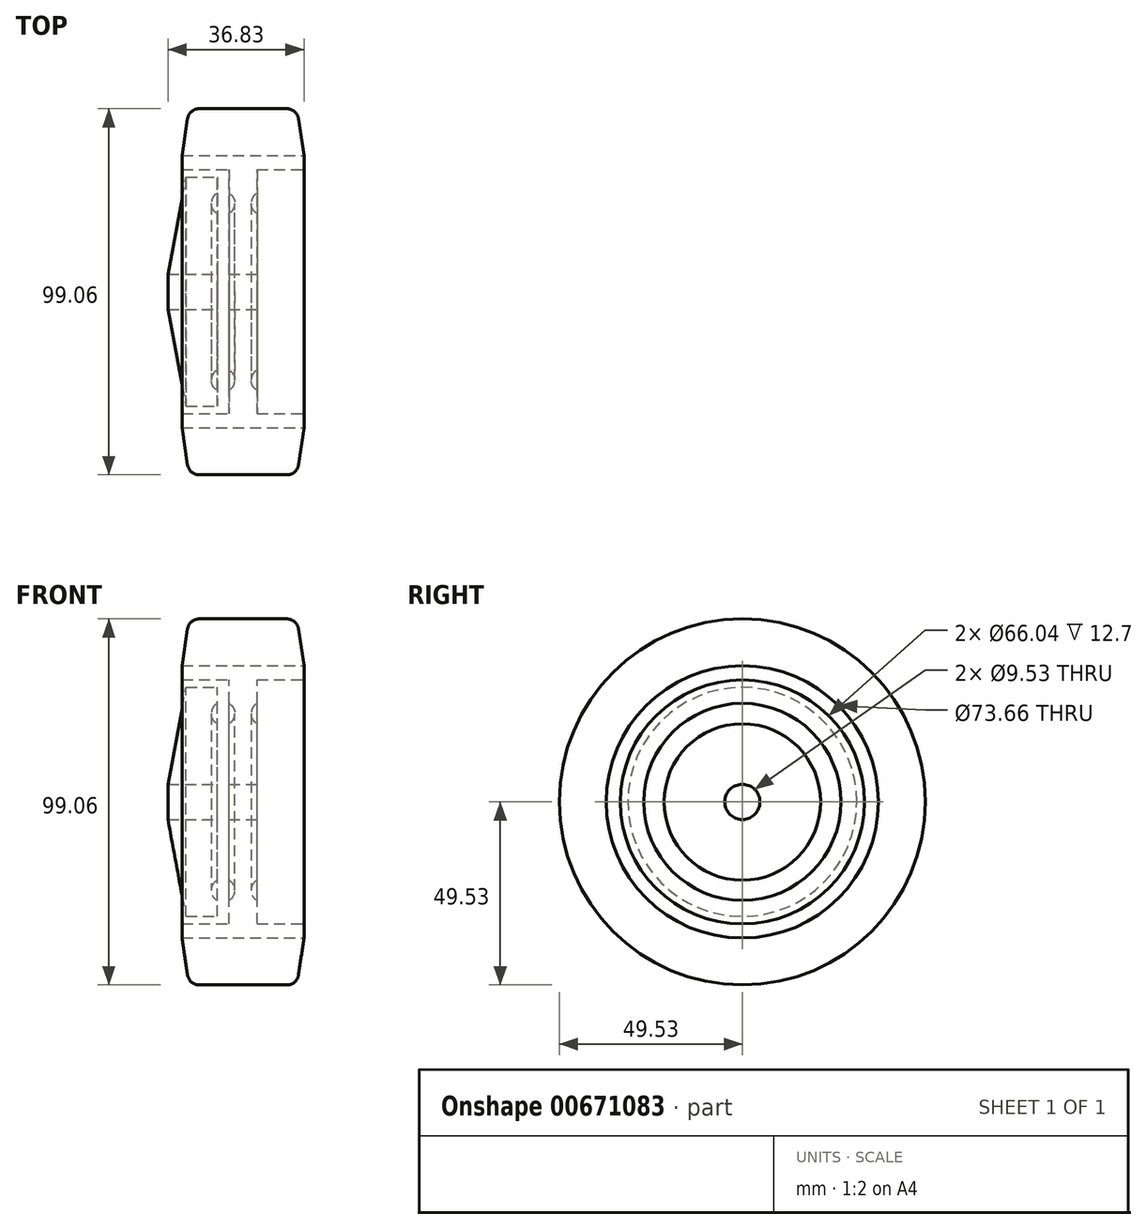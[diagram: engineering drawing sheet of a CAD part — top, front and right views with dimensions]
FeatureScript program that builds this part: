
annotation { "Feature Type Name" : "Feature", "Feature Type Description" : "" }
export const myFeature = defineFeature(function(context is Context, id is Id, definition is map)
    precondition{}
    {
        {
            var Q0;
            Q0=qCreatedBy(makeId("Top.planeOp"),FACE);
            var sketch = newSketch(context, id + "F0", { "sketchPlane" : qUnion([Q0])});
            skLineSegment(sketch, "E0", {"start": v(163.96, 0) * mm, "end": v(-163.85, 0) * mm, "construction": true});
            skSolve(sketch);
        }
        {
            var Q0;
            Q0=qCreatedBy(makeId("Front.planeOp"),FACE);
            var sketch = newSketch(context, id + "F1", { "sketchPlane" : qUnion([Q0])});
            skLineSegment(sketch, "E1", {"start": v(0, 0) * mm, "end": v(0, 60.9) * mm, "construction": true});
            skLineSegment(sketch, "E2", {"start": v(0, 49.53) * mm, "end": v(14.6, 49.53) * mm});
            skLineSegment(sketch, "E3", {"start": v(14.6, 49.53) * mm, "end": v(16.51, 36.83) * mm});
            skLineSegment(sketch, "E4", {"start": v(16.51, 36.83) * mm, "end": v(0, 36.83) * mm});
            skLineSegment(sketch, "E5.MirrorCS", {"start": v(0, 49.53) * mm, "end": v(-14.6, 49.53) * mm});
            skLineSegment(sketch, "E6.MirrorCS", {"start": v(-14.6, 49.53) * mm, "end": v(-16.51, 36.83) * mm});
            skLineSegment(sketch, "E7.MirrorCS", {"start": v(-16.51, 36.83) * mm, "end": v(0, 36.83) * mm});
            skSolve(sketch);
        }
        {
            var Q0;
            Q0=makeQuery(id+"F1.imprint","IMPRINT",FACE,{"disambiguationData":[TD([[makeQuery(id+"F1.imprint","IMPRINT",EDGE,{"derivedFrom":sQuery(id+"F1.wireOp",EDGE,"E2")}),-1.0]])]});
            var Q1;
            Q1=sQuery(id+"F0.wireOp",EDGE,"E0");
            revolve(context, id + "F2", {"entities" : qUnion([Q0]), "axis" : qUnion([Q1]), "revolveType" : RevolveType.FULL});
        }
        {
            var Q0;
            Q0=makeQuery(id+"F2.opRevolve","SWEPT_EDGE",EDGE,{"disambiguationData":[OSD([sQuery(id+"F1.wireOp",EDGE,"E5.MirrorCS"),sQuery(id+"F1.wireOp",EDGE,"E6.MirrorCS")])]});
            var Q1;
            Q1=makeQuery(id+"F2.opRevolve","SWEPT_EDGE",EDGE,{"disambiguationData":[OSD([sQuery(id+"F1.wireOp",EDGE,"E2"),sQuery(id+"F1.wireOp",EDGE,"E3")])]});
            fillet(context, id + "F3", {"entities" : qUnion([Q0, Q1]), "radius" : 3.17 * mm, "tangentPropagation" : true, "allowEdgeOverflow" : false});
        }
        {
            var Q0;
            Q0=qCreatedBy(makeId("Front.planeOp"),FACE);
            var sketch = newSketch(context, id + "F4", { "sketchPlane" : qUnion([Q0])});
            skPoint(sketch, "E8.0", {"position": v(16.51, 36.83) * mm});
            skPoint(sketch, "E9.0", {"position": v(0, 36.83) * mm});
            skLineSegment(sketch, "E10", {"start": v(0, 36.83) * mm, "end": v(16.51, 36.83) * mm});
            skLineSegment(sketch, "E11", {"start": v(16.51, 33.02) * mm, "end": v(16.51, 36.83) * mm});
            skLineSegment(sketch, "E12", {"start": v(16.51, 33.02) * mm, "end": v(3.81, 33.02) * mm});
            skLineSegment(sketch, "E13", {"start": v(3.81, 33.02) * mm, "end": v(3.81, 26.67) * mm});
            skArc(sketch, "E14", {"start": v(3.8, 26.67) * mm, "mid": v(2.22, 23.92) * mm, "end": v(3.81, 21.17) * mm});
            skLineSegment(sketch, "E15.MirrorCS", {"start": v(0, 36.83) * mm, "end": v(-16.51, 36.83) * mm});
            skLineSegment(sketch, "E16.MirrorCS", {"start": v(-16.51, 33.02) * mm, "end": v(-16.51, 36.83) * mm});
            skLineSegment(sketch, "E17.MirrorCS", {"start": v(-16.51, 33.02) * mm, "end": v(-3.81, 33.02) * mm});
            skLineSegment(sketch, "E18.MirrorCS", {"start": v(-3.81, 33.02) * mm, "end": v(-3.81, 26.67) * mm});
            skArc(sketch, "E19.MirrorCS", {"start": v(-3.8, 26.67) * mm, "mid": v(-2.22, 23.92) * mm, "end": v(-3.81, 21.17) * mm});
            skLineSegment(sketch, "E20", {"start": v(3.81, 21.17) * mm, "end": v(3.81, 4.76) * mm});
            skLineSegment(sketch, "E21", {"start": v(3.81, 4.76) * mm, "end": v(0, 4.76) * mm});
            skLineSegment(sketch, "E22.MirrorCS", {"start": v(-3.81, 21.17) * mm, "end": v(-3.81, 4.76) * mm});
            skLineSegment(sketch, "E23.MirrorCS", {"start": v(-3.81, 4.76) * mm, "end": v(0, 4.76) * mm});
            skSolve(sketch);
        }
        {
            var Q0;
            Q0=makeQuery(id+"F4.imprint","IMPRINT",FACE,{"disambiguationData":[TD([[makeQuery(id+"F4.imprint","IMPRINT",EDGE,{"derivedFrom":sQuery(id+"F4.wireOp",EDGE,"E10")}),-1.0]])]});
            var Q1;
            Q1=sQuery(id+"F0.wireOp",EDGE,"E0");
            revolve(context, id + "F5", {"entities" : qUnion([Q0]), "axis" : qUnion([Q1]), "revolveType" : RevolveType.FULL});
        }
        {
            var Q0;
            Q0=qCreatedBy(makeId("Front.planeOp"),FACE);
            var sketch = newSketch(context, id + "F6", { "sketchPlane" : qUnion([Q0])});
            skLineSegment(sketch, "E24", {"start": v(-6.99, 30.99) * mm, "end": v(-15.44, 30.99) * mm});
            skLineSegment(sketch, "E25", {"start": v(-15.44, 30.99) * mm, "end": v(-20.32, 4.76) * mm});
            skLineSegment(sketch, "E26", {"start": v(-20.32, 4.76) * mm, "end": v(-6.99, 4.76) * mm});
            skLineSegment(sketch, "E27", {"start": v(-6.99, 4.76) * mm, "end": v(-6.99, 21.17) * mm});
            skPoint(sketch, "E28.0", {"position": v(-3.8, 26.67) * mm});
            skLineSegment(sketch, "E29", {"start": v(-3.8, 26.67) * mm, "end": v(-13.53, 26.67) * mm, "construction": true});
            skPoint(sketch, "E30.0", {"position": v(-3.81, 21.17) * mm});
            skLineSegment(sketch, "E31", {"start": v(-3.81, 21.17) * mm, "end": v(-13.78, 21.17) * mm, "construction": true});
            skArc(sketch, "E32", {"start": v(-6.99, 26.67) * mm, "mid": v(-8.57, 23.92) * mm, "end": v(-6.99, 21.17) * mm});
            skLineSegment(sketch, "E33.trimOffspring", {"start": v(-6.99, 26.67) * mm, "end": v(-6.99, 30.99) * mm});
            skSolve(sketch);
        }
        {
            var Q0;
            Q0 = qSketchRegion(id + "F6", true);
            var Q1;
            Q1=sQuery(id+"F0.wireOp",EDGE,"E0");
            revolve(context, id + "F7", {"entities" : qUnion([Q0]), "axis" : qUnion([Q1]), "revolveType" : RevolveType.FULL});
        }
    });
